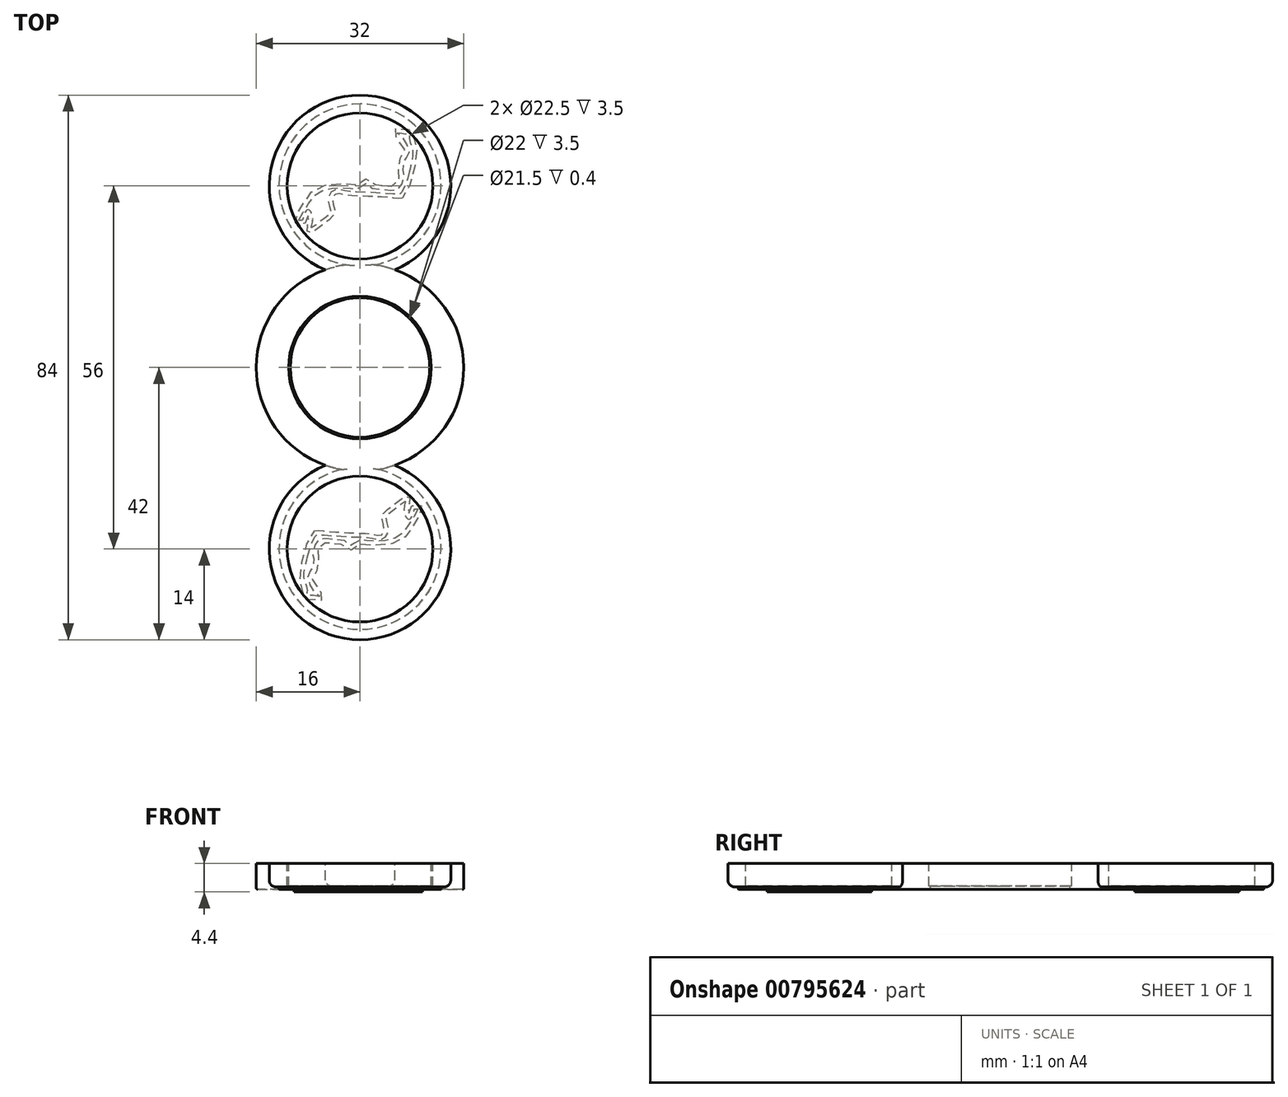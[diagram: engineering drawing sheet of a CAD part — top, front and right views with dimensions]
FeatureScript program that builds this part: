
annotation { "Feature Type Name" : "Feature", "Feature Type Description" : "" }
export const myFeature = defineFeature(function(context is Context, id is Id, definition is map)
    precondition{}
    {
        {
            var Q0;
            Q0=qCreatedBy(makeId("Top.planeOp"),FACE);
            var sketch = newSketch(context, id + "F0", { "sketchPlane" : qUnion([Q0])});
            skCircle(sketch, "E0", {"center": v(0, 0) * mm, "radius": 16 * mm});
            skCircle(sketch, "E1", {"center": v(0, 0) * mm, "radius": 11 * mm});
            skCircle(sketch, "E2", {"center": v(0, 0) * mm, "radius": 10.75 * mm});
            skCircle(sketch, "E3", {"center": v(0, 28) * mm, "radius": 14 * mm});
            skCircle(sketch, "E4", {"center": v(0, 28) * mm, "radius": 11.25 * mm});
            skCircle(sketch, "E5", {"center": v(0, 0) * mm, "radius": 40 * mm, "construction": true});
            skCircle(sketch, "E6", {"center": v(0, -28) * mm, "radius": 14 * mm});
            skCircle(sketch, "E7", {"center": v(0, -28) * mm, "radius": 11.25 * mm});
            skSolve(sketch);
        }
        {
            var Q0;
            Q0=makeQuery(id+"F0.imprint","IMPRINT",FACE,{"disambiguationData":[TD([[makeQuery(id+"F0.imprint","IMPRINT",EDGE,{"derivedFrom":sQuery(id+"F0.wireOp",EDGE,"E1")}),-1.0]])]});
            var Q1;
            {var subQ0=sQuery(id+"F0.wireOp",EDGE,"E3");var subQ1=sQuery(id+"F0.wireOp",EDGE,"E0");var subQ2=makeQuery(id+"F0.imprint","INTERSECT",VERTEX,{"disambiguationData":[OD(0.0)],"derivedFrom":[subQ1,subQ0]});Q1=makeQuery(id+"F0.imprint","IMPRINT",FACE,{"disambiguationData":[TD([[makeQuery(id+"F0.imprint","IMPRINT",EDGE,{"disambiguationData":[TD([[subQ2,1.0]])],"derivedFrom":subQ1}),1.0]])]});}
            var Q2;
            {var subQ0=sQuery(id+"F0.wireOp",EDGE,"E6");var subQ1=sQuery(id+"F0.wireOp",EDGE,"E0");var subQ2=makeQuery(id+"F0.imprint","INTERSECT",VERTEX,{"disambiguationData":[OD(0.0)],"derivedFrom":[subQ1,subQ0]});Q2=makeQuery(id+"F0.imprint","IMPRINT",FACE,{"disambiguationData":[TD([[makeQuery(id+"F0.imprint","IMPRINT",EDGE,{"disambiguationData":[TD([[subQ2,-1.0]])],"derivedFrom":subQ1}),1.0]])]});}
            extrude(context, id + "F1", {"entities" : qUnion([Q0, Q1, Q2]), "oppositeDirection" : true, "depth" : 4 * mm, "offsetDistance" : 25 * mm});
        }
        {
            var Q0;
            Q0=makeQuery(id+"F0.imprint","IMPRINT",FACE,{"disambiguationData":[TD([[makeQuery(id+"F0.imprint","IMPRINT",EDGE,{"derivedFrom":sQuery(id+"F0.wireOp",EDGE,"E1")}),1.0]])]});
            extrude(context, id + "F2", {"entities" : qUnion([Q0]), "operationType" : NewBodyOperationType.ADD, "oppositeDirection" : true, "depth" : 4 * mm, "offsetDistance" : 25 * mm, "hasSecondDirection" : true, "secondDirectionOppositeDirection" : true, "secondDirectionDepth" : 3.5 * mm});
        }
        {
            var Q0;
            Q0=makeQuery(id+"F2.opExtrude","CAP_EDGE",EDGE,{"disambiguationData":[OSD([sQuery(id+"F0.wireOp",EDGE,"E1")])],"isStart":true});
            var Q1;
            Q1=makeQuery(id+"F2.opExtrude","CAP_EDGE",EDGE,{"disambiguationData":[OSD([sQuery(id+"F0.wireOp",EDGE,"E2")])],"isStart":false});
            fillet(context, id + "F3", {"entities" : qUnion([Q0, Q1]), "radius" : 0.1 * mm, "tangentPropagation" : true, "allowEdgeOverflow" : false});
        }
        {
            var Q0;
            Q0=makeQuery(id+"F0.imprint","IMPRINT",FACE,{"disambiguationData":[TD([[makeQuery(id+"F0.imprint","IMPRINT",EDGE,{"derivedFrom":sQuery(id+"F0.wireOp",EDGE,"E7")}),-1.0]])]});
            var Q1;
            Q1=makeQuery(id+"F0.imprint","IMPRINT",FACE,{"disambiguationData":[TD([[makeQuery(id+"F0.imprint","IMPRINT",EDGE,{"derivedFrom":sQuery(id+"F0.wireOp",EDGE,"E4")}),-1.0]])]});
            extrude(context, id + "F4", {"entities" : qUnion([Q0, Q1]), "operationType" : NewBodyOperationType.ADD, "oppositeDirection" : true, "depth" : 3.6 * mm, "offsetDistance" : 25 * mm});
        }
        {
            var Q0;
            Q0=qCreatedBy(makeId("Top.planeOp"),FACE);
            var sketch = newSketch(context, id + "F5", { "sketchPlane" : qUnion([Q0])});
            skCircle(sketch, "E8", {"center": v(0, 28.15) * mm, "radius": 12.5 * mm});
            skCircle(sketch, "E9", {"center": v(0, -27.9) * mm, "radius": 12.5 * mm});
            skSolve(sketch);
        }
        {
            var Q0;
            Q0=makeQuery(id+"F5.imprint","IMPRINT",FACE,{"disambiguationData":[TD([[makeQuery(id+"F5.imprint","IMPRINT",EDGE,{"derivedFrom":sQuery(id+"F5.wireOp",EDGE,"E8")}),1.0]])]});
            var Q1;
            Q1=makeQuery(id+"F5.imprint","IMPRINT",FACE,{"disambiguationData":[TD([[makeQuery(id+"F5.imprint","IMPRINT",EDGE,{"derivedFrom":sQuery(id+"F5.wireOp",EDGE,"E9")}),1.0]])]});
            extrude(context, id + "F6", {"entities" : qUnion([Q0, Q1]), "operationType" : NewBodyOperationType.ADD, "oppositeDirection" : true, "depth" : 4 * mm, "offsetDistance" : 25 * mm, "hasSecondDirection" : true, "secondDirectionOppositeDirection" : true, "secondDirectionDepth" : 3.5 * mm});
        }
        {
            var Q0;
            Q0=makeQuery(id+"F6.boolean.opBoolean","SPLIT",EDGE,{"disambiguationData":[OD(1.0)],"derivedFrom":makeQuery(id+"F1.opExtrude","CAP_EDGE",EDGE,{"disambiguationData":[OSD([sQuery(id+"F0.wireOp",EDGE,"E0")])],"isStart":false})});
            var Q1;
            Q1=makeQuery(id+"F6.boolean.opBoolean","SPLIT",EDGE,{"disambiguationData":[OD(0.0)],"derivedFrom":makeQuery(id+"F1.opExtrude","CAP_EDGE",EDGE,{"disambiguationData":[OSD([sQuery(id+"F0.wireOp",EDGE,"E0")])],"isStart":false})});
            fillet(context, id + "F7", {"entities" : qUnion([Q0, Q1]), "radius" : 0.2 * mm, "tangentPropagation" : true, "allowEdgeOverflow" : false});
        }
        {
            var Q0;
            Q0=makeQuery(id+"F6.boolean.opBoolean","INTERSECT",EDGE,{"derivedFrom":[makeQuery(id+"F4.opExtrude","CAP_FACE",FACE,{"disambiguationData":[OSD([sQuery(id+"F0.wireOp",EDGE,"E0"),sQuery(id+"F0.wireOp",EDGE,"E3"),sQuery(id+"F0.wireOp",EDGE,"E4")])],"isStart":false}),makeQuery(id+"F6.opExtrude","SWEPT_FACE",FACE,{"disambiguationData":[OSD([sQuery(id+"F5.wireOp",EDGE,"E8")])]})]});
            var Q1;
            Q1=makeQuery(id+"F6.boolean.opBoolean","INTERSECT",EDGE,{"derivedFrom":[makeQuery(id+"F4.opExtrude","CAP_FACE",FACE,{"disambiguationData":[OSD([sQuery(id+"F0.wireOp",EDGE,"E0"),sQuery(id+"F0.wireOp",EDGE,"E6"),sQuery(id+"F0.wireOp",EDGE,"E7")])],"isStart":false}),makeQuery(id+"F6.opExtrude","SWEPT_FACE",FACE,{"disambiguationData":[OSD([sQuery(id+"F5.wireOp",EDGE,"E9")])]})]});
            fillet(context, id + "F8", {"entities" : qUnion([Q0, Q1]), "radius" : 0.2 * mm, "tangentPropagation" : true, "allowEdgeOverflow" : false});
        }
        {
            var Q0;
            Q0=makeQuery(id+"F4.opExtrude","CAP_EDGE",EDGE,{"disambiguationData":[OSD([sQuery(id+"F0.wireOp",EDGE,"E3")])],"isStart":false});
            var Q1;
            Q1=makeQuery(id+"F4.opExtrude","CAP_EDGE",EDGE,{"disambiguationData":[OSD([sQuery(id+"F0.wireOp",EDGE,"E6")])],"isStart":false});
            fillet(context, id + "F9", {"entities" : qUnion([Q0, Q1]), "radius" : 1 * mm, "tangentPropagation" : true, "allowEdgeOverflow" : false});
        }
        {
            var Q0;
            Q0=makeQuery(id+"F6.opExtrude","CAP_EDGE",EDGE,{"disambiguationData":[OSD([sQuery(id+"F5.wireOp",EDGE,"E9")])],"isStart":false});
            var Q1;
            Q1=makeQuery(id+"F6.opExtrude","CAP_EDGE",EDGE,{"disambiguationData":[OSD([sQuery(id+"F5.wireOp",EDGE,"E8")])],"isStart":false});
            fillet(context, id + "F10", {"entities" : qUnion([Q0, Q1]), "radius" : 0.1 * mm, "tangentPropagation" : true, "allowEdgeOverflow" : false});
        }
        {
            var Q0;
            Q0=qCreatedBy(makeId("Top.planeOp"),FACE);
            cPlane(context, id + "F11", {"entities" : qUnion([Q0]), "cplaneType" : CPlaneType.OFFSET, "offset" : 3.6 * mm, "oppositeDirection" : true, "width" : 150 * mm, "height" : 150 * mm});
        }
        {
            var Q0;
            Q0=qCreatedBy(id+"F11.planeOp",FACE);
            var sketch = newSketch(context, id + "F12", { "sketchPlane" : qUnion([Q0])});
            skFitSpline(sketch, "E10", {"points": [v(-7.02, -25.2) * mm, v(-6.88, -25.17) * mm, v(-6.76, -25.15) * mm, v(-6.56, -25.14) * mm, v(-6.38, -25.14) * mm, v(-6.2, -25.18) * mm, v(-5.94, -25.2) * mm, v(-5.64, -25.22) * mm, v(-5.24, -25.25) * mm, v(-4.89, -25.28) * mm, v(-4.45, -25.32) * mm, v(-4.06, -25.35) * mm, v(-3.66, -25.37) * mm, v(-3.22, -25.4) * mm, v(-2.82, -25.43) * mm, v(-2.42, -25.46) * mm, v(-1.92, -25.47) * mm, v(-1.37, -25.5) * mm, v(-0.61, -25.53) * mm, v(0.27, -25.54) * mm, v(0.81, -25.57) * mm, v(1.23, -25.61) * mm, v(1.64, -25.69) * mm, v(2.06, -25.73) * mm, v(2.43, -25.8) * mm, v(2.74, -25.87) * mm, v(2.94, -25.87) * mm, v(3.1, -25.86) * mm, v(3.28, -25.82) * mm, v(3.47, -25.72) * mm, v(3.58, -25.54) * mm, v(3.7, -25.32) * mm, v(3.77, -24.95) * mm, v(3.76, -24.57) * mm, v(3.6, -24.12) * mm, v(3.46, -23.76) * mm, v(3.39, -23.37) * mm, v(3.41, -23.12) * mm, v(3.5, -22.81) * mm, v(3.63, -22.5) * mm, v(3.76, -22.31) * mm, v(4, -22.07) * mm, v(4.49, -21.67) * mm, v(5.1, -21.22) * mm, v(5.7, -20.74) * mm, v(6.22, -20.36) * mm, v(6.74, -20.02) * mm, v(6.98, -19.9) * mm, v(7.17, -19.84) * mm, v(7.34, -19.84) * mm, v(7.5, -19.91) * mm, v(7.63, -20.08) * mm, v(7.7, -20.24) * mm, v(7.68, -20.51) * mm, v(7.6, -20.85) * mm, v(7.55, -21.15) * mm, v(7.48, -21.46) * mm, v(7.44, -21.75) * mm, v(7.42, -22.02) * mm, v(7.45, -22.33) * mm, v(7.53, -22.48) * mm], "startDerivative": vector(12.87, 4) * mm, "endDerivative": vector(8.17, -11.49) * mm});
            skFitSpline(sketch, "E11", {"points": [v(7.53, -22.48) * mm, v(7.62, -22.28) * mm, v(7.67, -22.1) * mm, v(7.71, -21.87) * mm, v(7.77, -21.65) * mm, v(7.86, -21.47) * mm, v(7.96, -21.35) * mm, v(8.11, -21.23) * mm, v(8.33, -21.2) * mm, v(8.62, -21.18) * mm, v(8.93, -21.2) * mm, v(9.21, -21.2) * mm, v(9.4, -21.3) * mm, v(9.53, -21.43) * mm, v(9.64, -21.59) * mm, v(9.64, -21.8) * mm, v(9.53, -22.09) * mm, v(9.32, -22.48) * mm, v(9.06, -22.98) * mm, v(8.81, -23.4) * mm, v(8.55, -23.86) * mm, v(8.34, -24.2) * mm, v(8.1, -24.61) * mm, v(7.87, -24.99) * mm, v(7.53, -25.52) * mm, v(7.32, -25.77) * mm, v(7.04, -26.07) * mm, v(6.6, -26.42) * mm, v(6.03, -26.79) * mm, v(5.54, -27) * mm, v(4.91, -27.2) * mm, v(4.22, -27.32) * mm, v(3.17, -27.41) * mm, v(2.14, -27.44) * mm, v(1.35, -27.4) * mm, v(0.67, -27.26) * mm, v(0.23, -27.23) * mm, v(-0.13, -27.28) * mm, v(-0.32, -27.45) * mm, v(-0.51, -27.74) * mm, v(-0.7, -27.96) * mm, v(-0.97, -28.14) * mm, v(-1.46, -28.16) * mm, v(-1.86, -27.93) * mm, v(-2.13, -27.66) * mm, v(-2.47, -27.4) * mm, v(-2.82, -27.3) * mm, v(-3.22, -27.25) * mm, v(-4, -27.17) * mm, v(-4.8, -27.11) * mm, v(-5.52, -27.05) * mm, v(-5.86, -27.03) * mm, v(-5.99, -27.06) * mm, v(-6.1, -27.16) * mm, v(-6.24, -27.37) * mm, v(-6.46, -27.89) * mm, v(-6.64, -28.4) * mm, v(-6.74, -28.78) * mm, v(-6.7, -28.97) * mm, v(-6.57, -29.18) * mm, v(-6.46, -29.38) * mm, v(-6.42, -29.63) * mm, v(-6.48, -30.12) * mm, v(-6.58, -30.56) * mm, v(-6.62, -31.03) * mm, v(-6.67, -31.33) * mm, v(-6.81, -31.64) * mm, v(-7.08, -31.86) * mm, v(-7.33, -32.02) * mm, v(-7.43, -32.13) * mm, v(-7.44, -32.42) * mm, v(-7.2, -33.1) * mm, v(-6.9, -33.83) * mm, v(-6.56, -34.3) * mm, v(-6, -34.69) * mm, v(-5.66, -34.97) * mm, v(-5.53, -35.2) * mm, v(-5.57, -35.57) * mm, v(-5.75, -35.8) * mm, v(-6.04, -35.94) * mm, v(-6.64, -35.94) * mm, v(-7.14, -35.84) * mm, v(-7.58, -35.76) * mm, v(-7.92, -35.76) * mm, v(-8.38, -35.75) * mm, v(-8.6, -35.67) * mm, v(-8.73, -35.52) * mm, v(-8.83, -35.24) * mm, v(-8.8, -34.93) * mm, v(-8.73, -34.64) * mm, v(-8.7, -34.4) * mm, v(-8.82, -33.93) * mm, v(-9.13, -33.05) * mm, v(-9.29, -32.28) * mm, v(-9.22, -31.45) * mm, v(-9.13, -30.93) * mm, v(-8.91, -29.83) * mm, v(-8.84, -29.61) * mm, v(-8.67, -28.8) * mm, v(-8.2, -27.32) * mm, v(-7.67, -26.12) * mm, v(-7.41, -25.59) * mm, v(-7.26, -25.36) * mm, v(-7.02, -25.2) * mm], "startDerivative": vector(13.18, 29.72) * mm, "endDerivative": vector(32.8, 17.75) * mm});
            skFitSpline(sketch, "E12", {"points": [v(-8.13, -29.3) * mm, v(-7.95, -28.62) * mm, v(-7.68, -27.78) * mm, v(-7.37, -26.96) * mm, v(-7.02, -26.23) * mm, v(-6.83, -25.86) * mm, v(-6.76, -25.75) * mm, v(-6.52, -25.77) * mm, v(-5.84, -25.8) * mm, v(-4.83, -25.9) * mm, v(-3.73, -25.96) * mm, v(-2.62, -26.04) * mm, v(-1.2, -26.12) * mm, v(0.33, -26.17) * mm, v(0.84, -26.2) * mm, v(1.3, -26.24) * mm, v(1.73, -26.31) * mm, v(2.16, -26.39) * mm, v(2.52, -26.46) * mm, v(2.76, -26.48) * mm, v(3.16, -26.47) * mm, v(3.46, -26.44) * mm, v(3.71, -26.33) * mm, v(3.97, -26.12) * mm, v(4.15, -25.86) * mm, v(4.3, -25.48) * mm, v(4.4, -25.02) * mm, v(4.4, -24.66) * mm, v(4.32, -24.26) * mm, v(4.19, -23.84) * mm, v(4.06, -23.56) * mm, v(4.04, -23.27) * mm, v(4.1, -22.93) * mm, v(4.25, -22.73) * mm, v(4.48, -22.48) * mm, v(4.89, -22.17) * mm, v(5.33, -21.8) * mm, v(5.73, -21.52) * mm, v(6.17, -21.17) * mm, v(6.46, -20.94) * mm, v(6.77, -20.73) * mm, v(6.99, -20.6) * mm], "startDerivative": vector(5.81, 22.58) * mm, "endDerivative": vector(11.7, 7.1) * mm});
            skFitSpline(sketch, "E13", {"points": [v(6.99, -20.6) * mm, v(6.99, -20.86) * mm, v(6.88, -21.18) * mm, v(6.82, -21.54) * mm, v(6.78, -21.9) * mm, v(6.8, -22.22) * mm, v(6.87, -22.48) * mm, v(6.99, -22.83) * mm, v(7.11, -23.11) * mm, v(7.23, -23.27) * mm, v(7.4, -23.37) * mm, v(7.62, -23.38) * mm, v(7.79, -23.28) * mm, v(7.94, -23.11) * mm, v(8.1, -22.76) * mm, v(8.2, -22.48) * mm, v(8.28, -22.17) * mm, v(8.37, -21.87) * mm, v(8.4, -21.8) * mm], "startDerivative": vector(0.5, -4.8) * mm, "endDerivative": vector(0.7, 2) * mm});
            skFitSpline(sketch, "E14", {"points": [v(8.4, -21.8) * mm, v(8.96, -21.8) * mm], "startDerivative": vector(0.57, 0) * mm, "endDerivative": vector(0.57, 0) * mm});
            skFitSpline(sketch, "E15", {"points": [v(8.96, -21.8) * mm, v(8.67, -22.31) * mm, v(8.4, -22.82) * mm, v(8, -23.51) * mm, v(7.53, -24.19) * mm, v(7.12, -24.86) * mm, v(6.65, -25.5) * mm, v(6.4, -25.71) * mm, v(5.87, -26.05) * mm, v(5.22, -26.38) * mm, v(4.45, -26.63) * mm, v(3.7, -26.76) * mm, v(2.93, -26.8) * mm, v(1.91, -26.79) * mm, v(1.44, -26.79) * mm, v(1.15, -26.73) * mm, v(0.78, -26.65) * mm, v(0.34, -26.64) * mm, v(0, -26.64) * mm, v(-0.24, -26.68) * mm, v(-0.51, -26.79) * mm, v(-0.7, -26.92) * mm, v(-0.85, -27.16) * mm, v(-0.99, -27.37) * mm, v(-1.16, -27.54) * mm, v(-1.35, -27.55) * mm, v(-1.66, -27.28) * mm, v(-2.05, -26.9) * mm, v(-2.32, -26.75) * mm, v(-2.73, -26.64) * mm, v(-3.26, -26.58) * mm, v(-3.7, -26.54) * mm, v(-4.56, -26.48) * mm, v(-5.4, -26.4) * mm, v(-5.99, -26.39) * mm, v(-6.2, -26.44) * mm, v(-6.4, -26.56) * mm, v(-6.57, -26.7) * mm, v(-6.73, -26.93) * mm, v(-6.97, -27.47) * mm, v(-7.16, -28.05) * mm, v(-7.3, -28.5) * mm, v(-7.34, -28.89) * mm, v(-7.3, -29.08) * mm, v(-7.2, -29.35) * mm, v(-7.12, -29.64) * mm, v(-7.19, -30.1) * mm, v(-7.2, -30.54) * mm, v(-7.23, -30.93) * mm, v(-7.26, -31.16) * mm, v(-7.45, -31.3) * mm, v(-7.7, -31.45) * mm, v(-7.95, -31.7) * mm, v(-8.07, -32.02) * mm, v(-8.08, -32.4) * mm, v(-8, -32.74) * mm, v(-7.86, -33.18) * mm, v(-7.56, -33.92) * mm, v(-7.23, -34.46) * mm, v(-6.97, -34.76) * mm, v(-6.71, -34.95) * mm, v(-6.34, -35.16) * mm, v(-6.18, -35.26) * mm], "startDerivative": vector(-15.7, -27.99) * mm, "endDerivative": vector(12.87, -8.44) * mm});
            skFitSpline(sketch, "E16", {"points": [v(-6.18, -35.26) * mm, v(-6.75, -35.26) * mm, v(-7.25, -35.18) * mm, v(-7.73, -35.13) * mm, v(-8.18, -35.14) * mm, v(-8.14, -34.82) * mm, v(-8.1, -34.56) * mm, v(-8.12, -34.23) * mm, v(-8.22, -33.8) * mm, v(-8.43, -33.18) * mm, v(-8.61, -32.53) * mm, v(-8.65, -32.03) * mm, v(-8.59, -31.45) * mm, v(-8.48, -30.9) * mm, v(-8.3, -30.07) * mm, v(-8.13, -29.3) * mm], "startDerivative": vector(-8.3, -0.53) * mm, "endDerivative": vector(2, 9.14) * mm});
            skFitSpline(sketch, "E17", {"points": [v(6.52, 26.13) * mm, v(6.39, 26.1) * mm, v(6.27, 26.08) * mm, v(6.06, 26.07) * mm, v(5.88, 26.07) * mm, v(5.71, 26.1) * mm, v(5.45, 26.13) * mm, v(5.14, 26.14) * mm, v(4.75, 26.18) * mm, v(4.4, 26.2) * mm, v(3.96, 26.25) * mm, v(3.56, 26.28) * mm, v(3.16, 26.3) * mm, v(2.73, 26.34) * mm, v(2.33, 26.36) * mm, v(1.93, 26.38) * mm, v(1.42, 26.4) * mm, v(0.88, 26.43) * mm, v(0.12, 26.46) * mm, v(-0.76, 26.47) * mm, v(-1.3, 26.5) * mm, v(-1.72, 26.54) * mm, v(-2.13, 26.61) * mm, v(-2.55, 26.66) * mm, v(-2.93, 26.73) * mm, v(-3.23, 26.8) * mm, v(-3.44, 26.8) * mm, v(-3.6, 26.78) * mm, v(-3.77, 26.75) * mm, v(-3.97, 26.65) * mm, v(-4.08, 26.47) * mm, v(-4.18, 26.25) * mm, v(-4.27, 25.88) * mm, v(-4.26, 25.5) * mm, v(-4.09, 25.04) * mm, v(-3.96, 24.7) * mm, v(-3.88, 24.3) * mm, v(-3.9, 24.05) * mm, v(-4, 23.74) * mm, v(-4.12, 23.44) * mm, v(-4.26, 23.24) * mm, v(-4.49, 23) * mm, v(-4.98, 22.6) * mm, v(-5.59, 22.14) * mm, v(-6.2, 21.67) * mm, v(-6.71, 21.28) * mm, v(-7.23, 20.95) * mm, v(-7.47, 20.83) * mm, v(-7.66, 20.77) * mm, v(-7.83, 20.77) * mm, v(-8, 20.84) * mm, v(-8.12, 21) * mm, v(-8.18, 21.16) * mm, v(-8.17, 21.44) * mm, v(-8.1, 21.78) * mm, v(-8.04, 22.08) * mm, v(-7.98, 22.38) * mm, v(-7.93, 22.67) * mm, v(-7.92, 22.95) * mm, v(-7.94, 23.25) * mm, v(-8.03, 23.41) * mm], "startDerivative": vector(-12.87, -4) * mm, "endDerivative": vector(-8.17, 11.49) * mm});
            skFitSpline(sketch, "E18", {"points": [v(-8.03, 23.41) * mm, v(-8.11, 23.2) * mm, v(-8.16, 23.03) * mm, v(-8.2, 22.8) * mm, v(-8.27, 22.58) * mm, v(-8.35, 22.4) * mm, v(-8.45, 22.28) * mm, v(-8.6, 22.15) * mm, v(-8.83, 22.12) * mm, v(-9.12, 22.1) * mm, v(-9.43, 22.12) * mm, v(-9.7, 22.13) * mm, v(-9.89, 22.23) * mm, v(-10.02, 22.36) * mm, v(-10.13, 22.52) * mm, v(-10.13, 22.74) * mm, v(-10.02, 23.01) * mm, v(-9.82, 23.41) * mm, v(-9.55, 23.9) * mm, v(-9.3, 24.33) * mm, v(-9.04, 24.79) * mm, v(-8.84, 25.13) * mm, v(-8.6, 25.54) * mm, v(-8.37, 25.91) * mm, v(-8.03, 26.44) * mm, v(-7.8, 26.7) * mm, v(-7.53, 27) * mm, v(-7.1, 27.35) * mm, v(-6.53, 27.71) * mm, v(-6.03, 27.92) * mm, v(-5.4, 28.14) * mm, v(-4.72, 28.25) * mm, v(-3.67, 28.34) * mm, v(-2.64, 28.37) * mm, v(-1.84, 28.32) * mm, v(-1.16, 28.18) * mm, v(-0.73, 28.16) * mm, v(-0.37, 28.2) * mm, v(-0.17, 28.38) * mm, v(0.02, 28.67) * mm, v(0.21, 28.89) * mm, v(0.48, 29.07) * mm, v(0.96, 29.1) * mm, v(1.36, 28.86) * mm, v(1.64, 28.58) * mm, v(1.98, 28.32) * mm, v(2.33, 28.22) * mm, v(2.73, 28.17) * mm, v(3.51, 28.1) * mm, v(4.3, 28.04) * mm, v(5.02, 27.98) * mm, v(5.36, 27.96) * mm, v(5.5, 28) * mm, v(5.62, 28.09) * mm, v(5.75, 28.3) * mm, v(5.97, 28.81) * mm, v(6.15, 29.33) * mm, v(6.24, 29.7) * mm, v(6.2, 29.9) * mm, v(6.07, 30.1) * mm, v(5.97, 30.31) * mm, v(5.93, 30.55) * mm, v(5.99, 31.05) * mm, v(6.09, 31.48) * mm, v(6.12, 31.96) * mm, v(6.17, 32.26) * mm, v(6.32, 32.57) * mm, v(6.58, 32.79) * mm, v(6.84, 32.95) * mm, v(6.93, 33.05) * mm, v(6.94, 33.34) * mm, v(6.72, 34.03) * mm, v(6.4, 34.76) * mm, v(6.06, 35.22) * mm, v(5.5, 35.62) * mm, v(5.17, 35.9) * mm, v(5.04, 36.14) * mm, v(5.07, 36.5) * mm, v(5.25, 36.73) * mm, v(5.54, 36.86) * mm, v(6.15, 36.86) * mm, v(6.64, 36.76) * mm, v(7.09, 36.7) * mm, v(7.43, 36.7) * mm, v(7.89, 36.68) * mm, v(8.1, 36.6) * mm, v(8.24, 36.45) * mm, v(8.33, 36.17) * mm, v(8.31, 35.86) * mm, v(8.24, 35.57) * mm, v(8.2, 35.33) * mm, v(8.32, 34.86) * mm, v(8.64, 33.97) * mm, v(8.8, 33.21) * mm, v(8.72, 32.38) * mm, v(8.64, 31.86) * mm, v(8.42, 30.76) * mm, v(8.35, 30.54) * mm, v(8.18, 29.73) * mm, v(7.7, 28.25) * mm, v(7.17, 27.05) * mm, v(6.92, 26.52) * mm, v(6.76, 26.29) * mm, v(6.52, 26.13) * mm], "startDerivative": vector(-13.18, -29.72) * mm, "endDerivative": vector(-32.8, -17.75) * mm});
            skFitSpline(sketch, "E19", {"points": [v(7.63, 30.23) * mm, v(7.45, 29.55) * mm, v(7.19, 28.7) * mm, v(6.87, 27.88) * mm, v(6.52, 27.16) * mm, v(6.34, 26.78) * mm, v(6.27, 26.67) * mm, v(6.03, 26.7) * mm, v(5.35, 26.73) * mm, v(4.33, 26.82) * mm, v(3.23, 26.9) * mm, v(2.12, 26.96) * mm, v(0.7, 27.05) * mm, v(-0.83, 27.1) * mm, v(-1.33, 27.12) * mm, v(-1.8, 27.17) * mm, v(-2.23, 27.24) * mm, v(-2.65, 27.31) * mm, v(-3.01, 27.39) * mm, v(-3.25, 27.41) * mm, v(-3.65, 27.4) * mm, v(-3.96, 27.36) * mm, v(-4.2, 27.25) * mm, v(-4.46, 27.05) * mm, v(-4.64, 26.78) * mm, v(-4.79, 26.4) * mm, v(-4.9, 25.95) * mm, v(-4.89, 25.59) * mm, v(-4.81, 25.19) * mm, v(-4.68, 24.77) * mm, v(-4.56, 24.49) * mm, v(-4.54, 24.2) * mm, v(-4.6, 23.86) * mm, v(-4.74, 23.65) * mm, v(-4.97, 23.41) * mm, v(-5.38, 23.1) * mm, v(-5.83, 22.74) * mm, v(-6.23, 22.44) * mm, v(-6.66, 22.1) * mm, v(-6.95, 21.86) * mm, v(-7.27, 21.66) * mm, v(-7.48, 21.53) * mm], "startDerivative": vector(-5.81, -22.58) * mm, "endDerivative": vector(-11.7, -7.1) * mm});
            skFitSpline(sketch, "E20", {"points": [v(-7.48, 21.53) * mm, v(-7.48, 21.8) * mm, v(-7.37, 22.1) * mm, v(-7.31, 22.47) * mm, v(-7.28, 22.82) * mm, v(-7.3, 23.15) * mm, v(-7.36, 23.41) * mm, v(-7.48, 23.76) * mm, v(-7.6, 24.04) * mm, v(-7.73, 24.2) * mm, v(-7.9, 24.3) * mm, v(-8.11, 24.3) * mm, v(-8.28, 24.2) * mm, v(-8.44, 24.04) * mm, v(-8.6, 23.69) * mm, v(-8.7, 23.41) * mm, v(-8.78, 23.1) * mm, v(-8.86, 22.8) * mm, v(-8.89, 22.72) * mm], "startDerivative": vector(-0.5, 4.8) * mm, "endDerivative": vector(-0.7, -2) * mm});
            skFitSpline(sketch, "E21", {"points": [v(-8.89, 22.72) * mm, v(-9.45, 22.72) * mm], "startDerivative": vector(-0.57, 0) * mm, "endDerivative": vector(-0.57, 0) * mm});
            skFitSpline(sketch, "E22", {"points": [v(-9.45, 22.72) * mm, v(-9.16, 23.24) * mm, v(-8.89, 23.75) * mm, v(-8.49, 24.44) * mm, v(-8.03, 25.12) * mm, v(-7.62, 25.8) * mm, v(-7.15, 26.42) * mm, v(-6.9, 26.64) * mm, v(-6.36, 26.98) * mm, v(-5.72, 27.3) * mm, v(-4.95, 27.56) * mm, v(-4.2, 27.69) * mm, v(-3.42, 27.73) * mm, v(-2.4, 27.71) * mm, v(-1.94, 27.71) * mm, v(-1.65, 27.65) * mm, v(-1.27, 27.58) * mm, v(-0.84, 27.57) * mm, v(-0.5, 27.57) * mm, v(-0.26, 27.6) * mm, v(0.02, 27.71) * mm, v(0.2, 27.85) * mm, v(0.36, 28.09) * mm, v(0.5, 28.3) * mm, v(0.66, 28.46) * mm, v(0.85, 28.47) * mm, v(1.17, 28.2) * mm, v(1.56, 27.83) * mm, v(1.82, 27.68) * mm, v(2.23, 27.57) * mm, v(2.76, 27.5) * mm, v(3.21, 27.47) * mm, v(4.07, 27.41) * mm, v(4.9, 27.33) * mm, v(5.5, 27.31) * mm, v(5.7, 27.36) * mm, v(5.9, 27.48) * mm, v(6.07, 27.63) * mm, v(6.23, 27.86) * mm, v(6.48, 28.4) * mm, v(6.67, 28.98) * mm, v(6.8, 29.43) * mm, v(6.85, 29.82) * mm, v(6.81, 30) * mm, v(6.7, 30.28) * mm, v(6.63, 30.57) * mm, v(6.7, 31.04) * mm, v(6.72, 31.47) * mm, v(6.74, 31.86) * mm, v(6.76, 32.09) * mm, v(6.96, 32.22) * mm, v(7.21, 32.38) * mm, v(7.45, 32.63) * mm, v(7.57, 32.95) * mm, v(7.59, 33.32) * mm, v(7.51, 33.67) * mm, v(7.37, 34.1) * mm, v(7.07, 34.84) * mm, v(6.74, 35.39) * mm, v(6.48, 35.69) * mm, v(6.22, 35.88) * mm, v(5.84, 36.09) * mm, v(5.69, 36.18) * mm], "startDerivative": vector(15.7, 27.99) * mm, "endDerivative": vector(-12.87, 8.44) * mm});
            skFitSpline(sketch, "E23", {"points": [v(5.69, 36.18) * mm, v(6.26, 36.18) * mm, v(6.76, 36.1) * mm, v(7.23, 36.06) * mm, v(7.68, 36.06) * mm, v(7.65, 35.75) * mm, v(7.6, 35.48) * mm, v(7.62, 35.16) * mm, v(7.73, 34.73) * mm, v(7.94, 34.1) * mm, v(8.12, 33.45) * mm, v(8.15, 32.96) * mm, v(8.1, 32.38) * mm, v(7.98, 31.83) * mm, v(7.8, 31) * mm, v(7.63, 30.23) * mm], "startDerivative": vector(8.3, 0.53) * mm, "endDerivative": vector(-2, -9.14) * mm});
            skSolve(sketch);
        }
        {
            var Q0;
            Q0=qSketchRegion(id+"F12",true);
            extrude(context, id + "F13", {"entities" : qUnion([Q0]), "operationType" : NewBodyOperationType.ADD, "oppositeDirection" : true, "depth" : 0.8 * mm, "offsetDistance" : 25 * mm});
        }
    });
